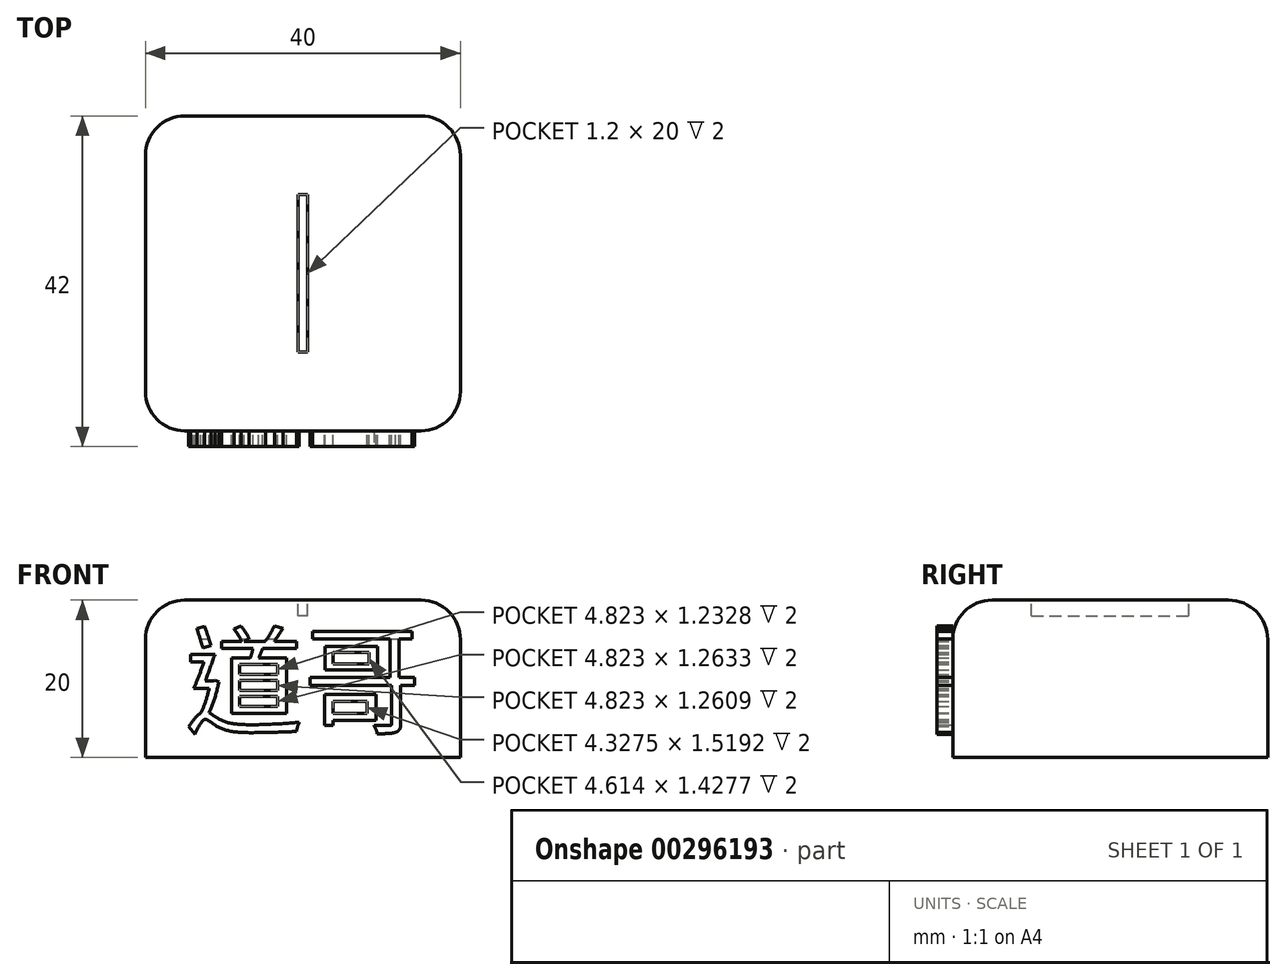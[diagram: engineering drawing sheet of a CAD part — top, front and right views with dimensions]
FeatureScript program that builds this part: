
annotation { "Feature Type Name" : "Feature", "Feature Type Description" : "" }
export const myFeature = defineFeature(function(context is Context, id is Id, definition is map)
    precondition{}
    {
        {
            var Q0;
            Q0=qCreatedBy(makeId("Top.planeOp"),FACE);
            var sketch = newSketch(context, id + "F0", { "sketchPlane" : qUnion([Q0])});
            skLineSegment(sketch, "E0.bottom", {"start": v(20, -20) * mm, "end": v(-20, -20) * mm});
            skLineSegment(sketch, "E0.top", {"start": v(20, 20) * mm, "end": v(-20, 20) * mm});
            skLineSegment(sketch, "E0.left", {"start": v(20, -20) * mm, "end": v(20, 20) * mm});
            skLineSegment(sketch, "E0.right", {"start": v(-20, -20) * mm, "end": v(-20, 20) * mm});
            skPoint(sketch, "E0.middle", {"position": v(0, 0) * mm});
            skLineSegment(sketch, "E1.bottom", {"start": v(0.6, -10) * mm, "end": v(-0.6, -10) * mm});
            skLineSegment(sketch, "E1.top", {"start": v(0.6, 10) * mm, "end": v(-0.6, 10) * mm});
            skLineSegment(sketch, "E1.left", {"start": v(0.6, -10) * mm, "end": v(0.6, 10) * mm});
            skLineSegment(sketch, "E1.right", {"start": v(-0.6, -10) * mm, "end": v(-0.6, 10) * mm});
            skSolve(sketch);
        }
        {
            var Q0;
            Q0=makeQuery(id+"F0.imprint","IMPRINT",FACE,{"disambiguationData":[TD([[makeQuery(id+"F0.imprint","IMPRINT",EDGE,{"derivedFrom":sQuery(id+"F0.wireOp",EDGE,"E0.bottom")}),-1.0]])]});
            var Q1;
            Q1=makeQuery(id+"F0.imprint","IMPRINT",FACE,{"disambiguationData":[TD([[makeQuery(id+"F0.imprint","IMPRINT",EDGE,{"derivedFrom":sQuery(id+"F0.wireOp",EDGE,"E1.bottom")}),-1.0]])]});
            extrude(context, id + "F1", {"entities" : qUnion([Q0, Q1]), "oppositeDirection" : true, "depth" : 20 * mm});
        }
        {
            var Q0;
            Q0=makeQuery(id+"F0.imprint","IMPRINT",FACE,{"disambiguationData":[TD([[makeQuery(id+"F0.imprint","IMPRINT",EDGE,{"derivedFrom":sQuery(id+"F0.wireOp",EDGE,"E1.bottom")}),-1.0]])]});
            extrude(context, id + "F2", {"entities" : qUnion([Q0]), "operationType" : NewBodyOperationType.REMOVE, "oppositeDirection" : true, "depth" : 2 * mm});
        }
        {
            var Q0;
            Q0=makeQuery(id+"F2.boolean.opBoolean","COPY",EDGE,{"derivedFrom":makeQuery(id+"F2.opExtrude","CAP_EDGE",EDGE,{"disambiguationData":[OSD([sQuery(id+"F0.wireOp",EDGE,"E1.left")])],"isStart":true})});
            var Q1;
            Q1=makeQuery(id+"F2.boolean.opBoolean","COPY",EDGE,{"derivedFrom":makeQuery(id+"F2.opExtrude","CAP_EDGE",EDGE,{"disambiguationData":[OSD([sQuery(id+"F0.wireOp",EDGE,"E1.right")])],"isStart":true})});
            var Q2;
            Q2=makeQuery(id+"F1.opExtrude","SWEPT_EDGE",EDGE,{"disambiguationData":[OSD([sQuery(id+"F0.wireOp",EDGE,"E0.bottom"),sQuery(id+"F0.wireOp",EDGE,"E0.left")])]});
            var Q3;
            Q3=makeQuery(id+"F1.opExtrude","SWEPT_EDGE",EDGE,{"disambiguationData":[OSD([sQuery(id+"F0.wireOp",EDGE,"E0.top"),sQuery(id+"F0.wireOp",EDGE,"E0.left")])]});
            var Q4;
            Q4=makeQuery(id+"F1.opExtrude","CAP_EDGE",EDGE,{"disambiguationData":[OSD([sQuery(id+"F0.wireOp",EDGE,"E0.left")])],"isStart":true});
            var Q5;
            Q5=makeQuery(id+"F1.opExtrude","SWEPT_EDGE",EDGE,{"disambiguationData":[OSD([sQuery(id+"F0.wireOp",EDGE,"E0.bottom"),sQuery(id+"F0.wireOp",EDGE,"E0.right")])]});
            var Q6;
            Q6=makeQuery(id+"F1.opExtrude","SWEPT_EDGE",EDGE,{"disambiguationData":[OSD([sQuery(id+"F0.wireOp",EDGE,"E0.top"),sQuery(id+"F0.wireOp",EDGE,"E0.right")])]});
            var Q7;
            Q7=makeQuery(id+"F1.opExtrude","CAP_EDGE",EDGE,{"disambiguationData":[OSD([sQuery(id+"F0.wireOp",EDGE,"E0.top")])],"isStart":true});
            var Q8;
            Q8=makeQuery(id+"F1.opExtrude","CAP_EDGE",EDGE,{"disambiguationData":[OSD([sQuery(id+"F0.wireOp",EDGE,"E0.right")])],"isStart":true});
            var Q9;
            Q9=makeQuery(id+"F1.opExtrude","CAP_EDGE",EDGE,{"disambiguationData":[OSD([sQuery(id+"F0.wireOp",EDGE,"E0.bottom")])],"isStart":true});
            fillet(context, id + "F3", {"entities" : qUnion([Q0, Q1, Q2, Q3, Q4, Q5, Q6, Q7, Q8, Q9]), "radius" : 5 * mm, "tangentPropagation" : true, "allowEdgeOverflow" : false});
        }
        {
            var Q0;
            Q0=makeQuery(id+"F1.opExtrude","SWEPT_FACE",FACE,{"disambiguationData":[OSD([sQuery(id+"F0.wireOp",EDGE,"E0.bottom")])]});
            var sketch = newSketch(context, id + "F4", { "sketchPlane" : qUnion([Q0])});
            skText(sketch, "E2", { "text": "道哥", "fontName": "NotoSansCJKtc-Regular.otf"});
            const initialGuessF4  = {"E2": [-0.015, -0.01582, 1, 0, 0.01082]};
            skSetInitialGuess(sketch, initialGuessF4);
            skSolve(sketch);
        }
        {
            var Q0;
            Q0=makeQuery(id+"F4.imprint","IMPRINT",FACE,{"disambiguationData":[TD([[makeQuery(id+"F4.imprint","IMPRINT",EDGE,{"derivedFrom":sQuery(id+"F4.wireOp",EDGE,"E2.sketch_text.stroke-0")}),1.0]])]});
            var Q1;
            Q1=makeQuery(id+"F4.imprint","IMPRINT",FACE,{"disambiguationData":[TD([[makeQuery(id+"F4.imprint","IMPRINT",EDGE,{"derivedFrom":sQuery(id+"F4.wireOp",EDGE,"E2.sketch_text.stroke-37")}),1.0]])]});
            var Q2;
            {var subQ0=sQuery(id+"F4.wireOp",EDGE,"E2.sketch_text.stroke-70");Q2=makeQuery(id+"F4.imprint","IMPRINT",FACE,{"disambiguationData":[TD([[makeQuery(id+"F4.imprint","IMPRINT",EDGE,{"derivedFrom":subQ0}),1.0]])]});}
            var Q3;
            Q3=makeQuery(id+"F4.imprint","IMPRINT",FACE,{"disambiguationData":[TD([[makeQuery(id+"F4.imprint","IMPRINT",EDGE,{"derivedFrom":sQuery(id+"F4.wireOp",EDGE,"E2.sketch_text.stroke-88")}),1.0]])]});
            var Q4;
            {var subQ0=sQuery(id+"F4.wireOp",EDGE,"E2.sketch_text.stroke-68");Q4=makeQuery(id+"F4.imprint","IMPRINT",FACE,{"disambiguationData":[TD([[makeQuery(id+"F4.imprint","IMPRINT",EDGE,{"derivedFrom":subQ0}),1.0]])]});}
            var Q5;
            Q5=makeQuery(id+"F4.imprint","IMPRINT",FACE,{"disambiguationData":[TD([[makeQuery(id+"F4.imprint","IMPRINT",EDGE,{"derivedFrom":sQuery(id+"F4.wireOp",EDGE,"E2.sketch_text.stroke-58")}),1.0]])]});
            var Q6;
            {var subQ5=sQuery(id+"F4.wireOp",EDGE,"E2.sketch_text.stroke-25");Q6=makeQuery(id+"F4.imprint","IMPRINT",FACE,{"disambiguationData":[TD([[makeQuery(id+"F4.imprint","IMPRINT",EDGE,{"derivedFrom":subQ5}),1.0]])]});}
            var Q7;
            {var subQ0=sQuery(id+"F4.wireOp",EDGE,"E2.sketch_text.stroke-21");Q7=makeQuery(id+"F4.imprint","IMPRINT",FACE,{"disambiguationData":[TD([[makeQuery(id+"F4.imprint","IMPRINT",EDGE,{"derivedFrom":subQ0}),1.0]])]});}
            extrude(context, id + "F5", {"entities" : qUnion([Q0, Q1, Q2, Q3, Q4, Q5, Q6, Q7]), "operationType" : NewBodyOperationType.ADD, "depth" : 2 * mm});
        }
        {
            var Q0;
            {var subQ0=sQuery(id+"F4.wireOp",EDGE,"E2.sketch_text.stroke-34");Q0=makeQuery(id+"F4.imprint","IMPRINT",FACE,{"disambiguationData":[TD([[makeQuery(id+"F4.imprint","IMPRINT",EDGE,{"derivedFrom":subQ0}),1.0]])]});}
            var Q1;
            {var subQ0=sQuery(id+"F4.wireOp",EDGE,"E2.sketch_text.stroke-36");Q1=makeQuery(id+"F4.imprint","IMPRINT",FACE,{"disambiguationData":[TD([[makeQuery(id+"F4.imprint","IMPRINT",EDGE,{"derivedFrom":subQ0}),1.0]])]});}
            extrude(context, id + "F6", {"entities" : qUnion([Q0, Q1]), "operationType" : NewBodyOperationType.ADD, "depth" : 2 * mm});
        }
    });
